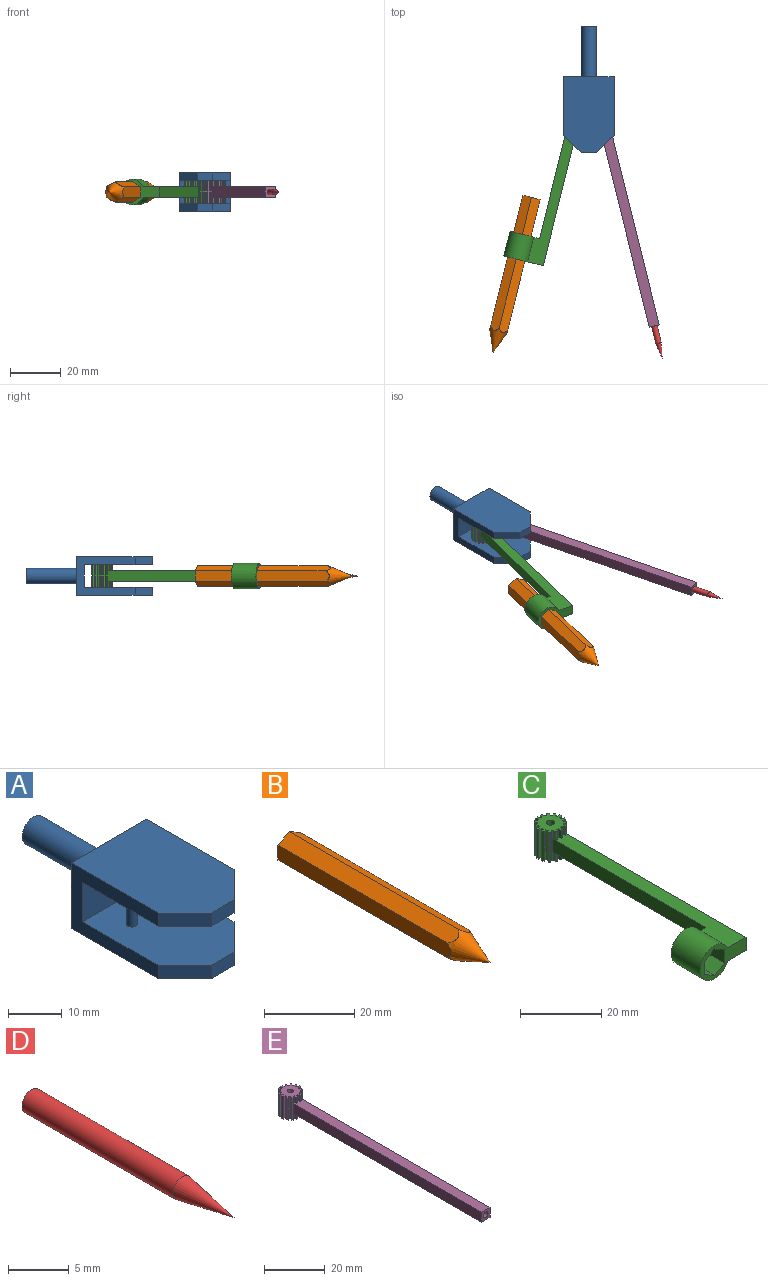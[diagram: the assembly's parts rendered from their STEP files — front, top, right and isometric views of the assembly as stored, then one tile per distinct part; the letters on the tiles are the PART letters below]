
ASSEMBLY  parts=5 mates=4
PART A: 18 faces, bbox 20x50x15 mm
  f0: plane 6x3mm, normal (0,-1,0), area 18mm2, adj f5,f7,f10,f11
  f1: plane 6x3mm, normal (0,-1,0), area 18mm2, adj f2,f6,f12,f13
  f2: plane 30x20mm, normal (0,0,1), area 551mm2, adj f1,f3,f4,f8,f12,f13
  f3: plane 23x15mm, normal (-1,0,0), area 165mm2, adj f2,f5,f6,f7,f8,f9,f10,f12
  f4: plane 23x15mm, normal (1,0,0), area 165mm2, adj f2,f5,f6,f7,f8,f9,f11,f13
  f5: plane 30x20mm, normal (0,0,-1), area 551mm2, adj f0,f3,f4,f8,f10,f11
  f6: plane 27x20mm, normal (0,0,-1), area 484.7mm2, adj f1,f3,f4,f9,f12,f13,f14,f15
  f7: plane 27x20mm, normal (0,0,1), area 484.7mm2, adj f0,f3,f4,f9,f10,f11,f14,f15
  f8: plane 20x15mm, normal (0,1,0), area 271.7mm2, adj f2,f3,f4,f5,f16
  f9: plane 20x9mm, normal (0,-1,0), area 180mm2, adj f3,f4,f6,f7
  f10: plane 7x7mm, normal (-0.71,-0.71,0), area 29.7mm2, adj f0,f3,f5,f7
  f11: plane 7x7mm, normal (0.71,-0.71,0), area 29.7mm2, adj f0,f4,f5,f7
  f12: plane 7x7mm, normal (-0.71,-0.71,0), area 29.7mm2, adj f1,f2,f3,f6
  f13: plane 7x7mm, normal (0.71,-0.71,0), area 29.7mm2, adj f1,f2,f4,f6
  f14: cylinder r=1mm len=9mm, axis (0,0,1), area 56.5mm2, adj f6,f7
  f15: cylinder r=1mm len=9mm, axis (0,0,1), area 56.5mm2, adj f6,f7
  f16: cylinder r=3mm len=20mm, axis (0,-1,0), area 377mm2, adj f8,f17
  f17: plane 6x6mm, normal (0,1,0), area 28.3mm2, adj f16
PART B: 8 faces, bbox 8x63x8 mm
  f0: plane 54.43x4mm, normal (1,0,0), area 215.9mm2, adj f1,f4,f6,f7
  f1: plane 54.43x3.46mm, normal (0.5,0,0.87), area 215.9mm2, adj f0,f2,f6,f7
  f2: plane 54.43x3.46mm, normal (-0.5,0,0.87), area 215.9mm2, adj f1,f3,f6,f7
  f3: plane 54.43x4mm, normal (-1,0,0), area 215.9mm2, adj f2,f5,f6,f7
  f4: plane 54.43x3.46mm, normal (0.5,0,-0.87), area 215.9mm2, adj f0,f5,f6,f7
  f5: plane 54.43x3.46mm, normal (-0.5,0,-0.87), area 215.9mm2, adj f3,f4,f6,f7
  f6: plane 8x6.93mm, normal (0,1,0), area 41.6mm2, adj f0,f1,f2,f3,f4,f5
  f7: cone r=40mm half-angle=22deg, axis (0,1,0), area 111mm2, adj f0,f1,f2,f3,f4,f5
PART C: 87 faces, bbox 18.1x70x10 mm
  f0: cylinder r=3.25mm len=9mm, axis (0,0,-1), area 3.5mm2, adj f1,f13,f27,f28,f73,f74,f78,f79
  f1: plane 2.5x0.79mm, normal (0.96,0.29,0), area 2.1mm2, adj f0,f2,f73,f78
  f2: plane 2.5x0.55mm, normal (0.41,-0.91,0), area 1.5mm2, adj f1,f3,f73,f78
  f3: plane 2.5x0.71mm, normal (-0.86,-0.51,0), area 2.1mm2, adj f2,f4,f73,f78
  f4: cylinder r=3.25mm len=2.5mm, axis (0,0,-1), area 1.4mm2, adj f3,f5,f73,f78
  f5: plane 2.5x0.82mm, normal (0.99,-0.12,0), area 2.1mm2, adj f4,f6,f73,f78
  f6: plane 2.5x0.6mm, normal (0,-1,0), area 1.5mm2, adj f5,f7,f73,f78
  f7: plane 2.5x0.82mm, normal (-0.99,-0.12,0), area 2.1mm2, adj f6,f8,f73,f78
  f8: cylinder r=3.25mm len=2.5mm, axis (0,0,-1), area 1.4mm2, adj f7,f9,f73,f78
  f9: plane 2.5x0.71mm, normal (0.86,-0.51,0), area 2.1mm2, adj f8,f10,f73,f78
  f10: plane 2.5x0.55mm, normal (-0.41,-0.91,0), area 1.5mm2, adj f9,f11,f73,f78
  f11: plane 2.5x0.79mm, normal (-0.96,0.29,0), area 2.1mm2, adj f10,f12,f73,f78
  f12: cylinder r=3.25mm len=9mm, axis (0,0,-1), area 3.5mm2, adj f11,f13,f38,f39,f73,f75,f78,f79
  f13: plane 8.12x8.07mm, normal (0,0,1), area 38.5mm2, adj f0,f12,f14,f15,f16,f17,f18,f19
  f14: plane 9x0.52mm, normal (0.87,0.5,0), area 5.4mm2, adj f13,f15,f71,f73
  f15: plane 9x0.66mm, normal (0.6,-0.8,0), area 7.5mm2, adj f13,f14,f16,f73
  f16: cylinder r=3.25mm len=9mm, axis (0,0,-1), area 5mm2, adj f13,f15,f17,f73
  f17: plane 9x0.83mm, normal (0.02,1,0), area 7.5mm2, adj f13,f16,f18,f73
  f18: plane 9x0.6mm, normal (0.99,0.1,0), area 5.4mm2, adj f13,f17,f19,f73
  f19: plane 9x0.81mm, normal (0.22,-0.97,0), area 7.5mm2, adj f13,f18,f20,f73
  f20: cylinder r=3.25mm len=9mm, axis (0,0,-1), area 5mm2, adj f13,f19,f21,f73
  f21: plane 9x0.75mm, normal (0.42,0.91,0), area 7.5mm2, adj f13,f20,f22,f73
  f22: plane 9x0.57mm, normal (0.95,-0.31,0), area 5.4mm2, adj f13,f21,f23,f73
  f23: plane 9x0.82mm, normal (-0.19,-0.98,0), area 7.5mm2, adj f13,f22,f24,f73
  f24: cylinder r=3.25mm len=9mm, axis (0,0,-1), area 5mm2, adj f13,f23,f25,f73
  f25: plane 9x0.63mm, normal (0.75,0.66,0), area 7.5mm2, adj f13,f24,f26,f73
  f26: plane 9x0.45mm, normal (0.74,-0.67,0), area 5.4mm2, adj f13,f25,f27,f73
  f27: plane 9x0.68mm, normal (-0.57,-0.82,0), area 7.5mm2, adj f0,f13,f26,f73
  f28: plane 2.5x0.79mm, normal (0.96,0.29,0), area 2.1mm2, adj f0,f13,f29,f79
  f29: plane 2.5x0.55mm, normal (0.41,-0.91,0), area 1.5mm2, adj f13,f28,f30,f79
  f30: plane 2.5x0.71mm, normal (-0.86,-0.51,0), area 2.1mm2, adj f13,f29,f31,f79
  f31: cylinder r=3.25mm len=2.5mm, axis (0,0,-1), area 1.4mm2, adj f13,f30,f32,f79
  f32: plane 2.5x0.82mm, normal (0.99,-0.12,0), area 2.1mm2, adj f13,f31,f33,f79
  f33: plane 2.5x0.6mm, normal (0,-1,0), area 1.5mm2, adj f13,f32,f34,f79
  f34: plane 2.5x0.82mm, normal (-0.99,-0.12,0), area 2.1mm2, adj f13,f33,f35,f79
  f35: cylinder r=3.25mm len=2.5mm, axis (0,0,-1), area 1.4mm2, adj f13,f34,f36,f79
  f36: plane 2.5x0.71mm, normal (0.86,-0.51,0), area 2.1mm2, adj f13,f35,f37,f79
  f37: plane 2.5x0.55mm, normal (-0.41,-0.91,0), area 1.5mm2, adj f13,f36,f38,f79
  f38: plane 2.5x0.79mm, normal (-0.96,0.29,0), area 2.1mm2, adj f12,f13,f37,f79
  f39: plane 9x0.68mm, normal (0.57,-0.82,0), area 7.5mm2, adj f12,f13,f40,f73
  f40: plane 9x0.45mm, normal (-0.74,-0.67,0), area 5.4mm2, adj f13,f39,f41,f73
  f41: plane 9x0.63mm, normal (-0.75,0.66,0), area 7.5mm2, adj f13,f40,f42,f73
  f42: cylinder r=3.25mm len=9mm, axis (0,0,-1), area 5mm2, adj f13,f41,f43,f73
  f43: plane 9x0.82mm, normal (0.19,-0.98,0), area 7.5mm2, adj f13,f42,f44,f73
  f44: plane 9x0.57mm, normal (-0.95,-0.31,0), area 5.4mm2, adj f13,f43,f45,f73
  f45: plane 9x0.75mm, normal (-0.42,0.91,0), area 7.5mm2, adj f13,f44,f46,f73
  f46: cylinder r=3.25mm len=9mm, axis (0,0,-1), area 5mm2, adj f13,f45,f47,f73
  f47: plane 9x0.81mm, normal (-0.22,-0.97,0), area 7.5mm2, adj f13,f46,f48,f73
  f48: plane 9x0.6mm, normal (-0.99,0.1,0), area 5.4mm2, adj f13,f47,f49,f73
  f49: plane 9x0.83mm, normal (-0.02,1,0), area 7.5mm2, adj f13,f48,f50,f73
  f50: cylinder r=3.25mm len=9mm, axis (0,0,-1), area 5mm2, adj f13,f49,f51,f73
  f51: plane 9x0.66mm, normal (-0.6,-0.8,0), area 7.5mm2, adj f13,f50,f52,f73
  f52: plane 9x0.52mm, normal (-0.87,0.5,0), area 5.4mm2, adj f13,f51,f53,f73
  f53: plane 9x0.76mm, normal (0.39,0.92,0), area 7.5mm2, adj f13,f52,f54,f73
  f54: cylinder r=3.25mm len=9mm, axis (0,0,-1), area 5mm2, adj f13,f53,f55,f73
  f55: plane 9x0.73mm, normal (-0.87,-0.49,0), area 7.5mm2, adj f13,f54,f56,f73
  f56: plane 9x0.49mm, normal (-0.59,0.81,0), area 5.4mm2, adj f13,f55,f57,f73
  f57: plane 9x0.61mm, normal (0.73,0.68,0), area 7.5mm2, adj f13,f56,f58,f73
  f58: cylinder r=3.25mm len=9mm, axis (0,0,-1), area 5mm2, adj f13,f57,f59,f73
  f59: plane 9x0.83mm, normal (-1,-0.09,0), area 7.5mm2, adj f13,f58,f60,f73
  f60: plane 9x0.59mm, normal (-0.21,0.98,0), area 5.4mm2, adj f13,f59,f61,f73
  f61: plane 9x0.79mm, normal (0.95,0.32,0), area 7.5mm2, adj f13,f60,f62,f73
  f62: cylinder r=3.25mm len=9mm, axis (0,0,-1), area 5mm2, adj f13,f61,f63,f73
  f63: plane 9x0.79mm, normal (-0.95,0.32,0), area 7.5mm2, adj f13,f62,f64,f73
  f64: plane 9x0.59mm, normal (0.21,0.98,0), area 5.4mm2, adj f13,f63,f65,f73
  f65: plane 9x0.83mm, normal (1,-0.09,0), area 7.5mm2, adj f13,f64,f66,f73
  f66: cylinder r=3.25mm len=9mm, axis (0,0,-1), area 5mm2, adj f13,f65,f67,f73
  f67: plane 9x0.61mm, normal (-0.73,0.68,0), area 7.5mm2, adj f13,f66,f68,f73
  f68: plane 9x0.49mm, normal (0.59,0.81,0), area 5.4mm2, adj f13,f67,f69,f73
  f69: plane 9x0.73mm, normal (0.87,-0.49,0), area 7.5mm2, adj f13,f68,f70,f73
  f70: cylinder r=3.25mm len=9mm, axis (0,0,-1), area 5mm2, adj f13,f69,f71,f73
  f71: plane 9x0.76mm, normal (-0.39,0.92,0), area 7.5mm2, adj f13,f14,f70,f73
  f72: cylinder r=1mm len=9mm, axis (0,0,-1), area 56.5mm2, adj f13,f73
  f73: plane 8.12x8.07mm, normal (0,0,-1), area 38.5mm2, adj f0,f1,f2,f3,f4,f5,f6,f7
  f74: plane 63.44x4mm, normal (1,0,0), area 253.8mm2, adj f0,f76,f78,f79
  f75: plane 53.44x4mm, normal (-1,0,0), area 213.8mm2, adj f12,f77,f78,f79
  f76: plane 16x10mm, normal (0,-1,0), area 61.5mm2, adj f74,f78,f79,f80,f81,f82,f83,f84
  f77: plane 12x10mm, normal (0,1,0), area 45.5mm2, adj f75,f78,f79,f80,f81,f82,f83,f84
  f78: plane 63.44x6.42mm, normal (0,0,-1), area 274.4mm2, adj f0,f1,f2,f3,f4,f5,f6,f7
  f79: plane 63.44x6.42mm, normal (0,0,1), area 274.4mm2, adj f0,f12,f28,f29,f30,f31,f32,f33
  f80: cylinder r=5mm len=10mm, axis (0,-1,0), area 273mm2, adj f76,f77,f78,f79
  f81: plane 10x3.46mm, normal (0.5,0,0.87), area 40mm2, adj f76,f77,f82,f84
  f82: plane 10x3.46mm, normal (-0.5,0,0.87), area 40mm2, adj f76,f77,f81,f83
  f83: plane 10x4mm, normal (-1,0,0), area 40mm2, adj f76,f77,f82,f85
  f84: plane 10x4mm, normal (1,0,0), area 40mm2, adj f76,f77,f81,f86
  f85: plane 10x3.46mm, normal (-0.5,0,-0.87), area 40mm2, adj f76,f77,f83,f86
  f86: plane 10x3.46mm, normal (0.5,0,-0.87), area 40mm2, adj f76,f77,f84,f85
PART D: 3 faces, bbox 2.2x23.5x2.2 mm
  f0: cone r=1.1mm half-angle=10.4deg, axis (0,1,0), area 21.1mm2, adj f1
  f1: cylinder r=1.1mm len=17.5mm, axis (0,-1,0), area 121mm2, adj f0,f2
  f2: plane 2.2x2.2mm, normal (0,1,0), area 3.8mm2, adj f1
PART E: 79 faces, bbox 8.1x95.1x9 mm
  f0: plane 9x0.61mm, normal (-0.73,-0.68,0), area 5mm2, adj f1,f11,f24,f25,f71,f73,f74,f75
  f1: cylinder r=3.25mm len=2.5mm, axis (0,0,-1), area 1.4mm2, adj f0,f2,f11,f74
  f2: plane 2.5x0.83mm, normal (1,0.09,0), area 2.1mm2, adj f1,f3,f11,f74
  f3: plane 2.5x0.59mm, normal (0.21,-0.98,0), area 1.5mm2, adj f2,f4,f11,f74
  f4: plane 2.5x0.79mm, normal (-0.95,-0.32,0), area 2.1mm2, adj f3,f5,f11,f74
  f5: cylinder r=3.25mm len=2.5mm, axis (0,0,-1), area 1.4mm2, adj f4,f6,f11,f74
  f6: plane 2.5x0.79mm, normal (0.95,-0.32,0), area 2.1mm2, adj f5,f7,f11,f74
  f7: plane 2.5x0.59mm, normal (-0.21,-0.98,0), area 1.5mm2, adj f6,f8,f11,f74
  f8: plane 2.5x0.83mm, normal (-1,0.09,0), area 2.1mm2, adj f7,f9,f11,f74
  f9: cylinder r=3.25mm len=2.5mm, axis (0,0,-1), area 1.4mm2, adj f8,f10,f11,f74
  f10: plane 9x0.61mm, normal (0.73,-0.68,0), area 5mm2, adj f9,f11,f33,f34,f71,f72,f74,f75
  f11: plane 8.12x8.07mm, normal (0,0,1), area 38.5mm2, adj f0,f1,f2,f3,f4,f5,f6,f7
  f12: plane 9x0.57mm, normal (0.95,0.31,0), area 5.4mm2, adj f11,f13,f69,f71
  f13: plane 9x0.75mm, normal (0.42,-0.91,0), area 7.5mm2, adj f11,f12,f14,f71
  f14: cylinder r=3.25mm len=9mm, axis (0,0,-1), area 5mm2, adj f11,f13,f15,f71
  f15: plane 9x0.81mm, normal (0.22,0.97,0), area 7.5mm2, adj f11,f14,f16,f71
  f16: plane 9x0.6mm, normal (0.99,-0.1,0), area 5.4mm2, adj f11,f15,f17,f71
  f17: plane 9x0.83mm, normal (0.02,-1,0), area 7.5mm2, adj f11,f16,f18,f71
  f18: cylinder r=3.25mm len=9mm, axis (0,0,-1), area 5mm2, adj f11,f17,f19,f71
  f19: plane 9x0.66mm, normal (0.6,0.8,0), area 7.5mm2, adj f11,f18,f20,f71
  f20: plane 9x0.52mm, normal (0.87,-0.5,0), area 5.4mm2, adj f11,f19,f21,f71
  f21: plane 9x0.76mm, normal (-0.39,-0.92,0), area 7.5mm2, adj f11,f20,f22,f71
  f22: cylinder r=3.25mm len=9mm, axis (0,0,-1), area 5mm2, adj f11,f21,f23,f71
  f23: plane 9x0.73mm, normal (0.87,0.49,0), area 7.5mm2, adj f11,f22,f24,f71
  f24: plane 9x0.49mm, normal (0.59,-0.81,0), area 5.4mm2, adj f0,f11,f23,f71
  f25: cylinder r=3.25mm len=2.5mm, axis (0,0,-1), area 1.4mm2, adj f0,f26,f71,f75
  f26: plane 2.5x0.83mm, normal (1,0.09,0), area 2.1mm2, adj f25,f27,f71,f75
  f27: plane 2.5x0.59mm, normal (0.21,-0.98,0), area 1.5mm2, adj f26,f28,f71,f75
  f28: plane 2.5x0.79mm, normal (-0.95,-0.32,0), area 2.1mm2, adj f27,f29,f71,f75
  f29: cylinder r=3.25mm len=2.5mm, axis (0,0,-1), area 1.4mm2, adj f28,f30,f71,f75
  f30: plane 2.5x0.79mm, normal (0.95,-0.32,0), area 2.1mm2, adj f29,f31,f71,f75
  f31: plane 2.5x0.59mm, normal (-0.21,-0.98,0), area 1.5mm2, adj f30,f32,f71,f75
  f32: plane 2.5x0.83mm, normal (-1,0.09,0), area 2.1mm2, adj f31,f33,f71,f75
  f33: cylinder r=3.25mm len=2.5mm, axis (0,0,-1), area 1.4mm2, adj f10,f32,f71,f75
  f34: plane 9x0.49mm, normal (-0.59,-0.81,0), area 5.4mm2, adj f10,f11,f35,f71
  f35: plane 9x0.73mm, normal (-0.87,0.49,0), area 7.5mm2, adj f11,f34,f36,f71
  f36: cylinder r=3.25mm len=9mm, axis (0,0,-1), area 5mm2, adj f11,f35,f37,f71
  f37: plane 9x0.76mm, normal (0.39,-0.92,0), area 7.5mm2, adj f11,f36,f38,f71
  f38: plane 9x0.52mm, normal (-0.87,-0.5,0), area 5.4mm2, adj f11,f37,f39,f71
  f39: plane 9x0.66mm, normal (-0.6,0.8,0), area 7.5mm2, adj f11,f38,f40,f71
  f40: cylinder r=3.25mm len=9mm, axis (0,0,-1), area 5mm2, adj f11,f39,f41,f71
  f41: plane 9x0.83mm, normal (-0.02,-1,0), area 7.5mm2, adj f11,f40,f42,f71
  f42: plane 9x0.6mm, normal (-0.99,-0.1,0), area 5.4mm2, adj f11,f41,f43,f71
  f43: plane 9x0.81mm, normal (-0.22,0.97,0), area 7.5mm2, adj f11,f42,f44,f71
  f44: cylinder r=3.25mm len=9mm, axis (0,0,-1), area 5mm2, adj f11,f43,f45,f71
  f45: plane 9x0.75mm, normal (-0.42,-0.91,0), area 7.5mm2, adj f11,f44,f46,f71
  f46: plane 9x0.57mm, normal (-0.95,0.31,0), area 5.4mm2, adj f11,f45,f47,f71
  f47: plane 9x0.82mm, normal (0.19,0.98,0), area 7.5mm2, adj f11,f46,f48,f71
  f48: cylinder r=3.25mm len=9mm, axis (0,0,-1), area 5mm2, adj f11,f47,f49,f71
  f49: plane 9x0.63mm, normal (-0.75,-0.66,0), area 7.5mm2, adj f11,f48,f50,f71
  f50: plane 9x0.45mm, normal (-0.74,0.67,0), area 5.4mm2, adj f11,f49,f51,f71
  f51: plane 9x0.68mm, normal (0.57,0.82,0), area 7.5mm2, adj f11,f50,f52,f71
  f52: cylinder r=3.25mm len=9mm, axis (0,0,-1), area 5mm2, adj f11,f51,f53,f71
  f53: plane 9x0.79mm, normal (-0.96,-0.29,0), area 7.5mm2, adj f11,f52,f54,f71
  f54: plane 9x0.55mm, normal (-0.41,0.91,0), area 5.4mm2, adj f11,f53,f55,f71
  f55: plane 9x0.71mm, normal (0.86,0.51,0), area 7.5mm2, adj f11,f54,f56,f71
  f56: cylinder r=3.25mm len=9mm, axis (0,0,-1), area 5mm2, adj f11,f55,f57,f71
  f57: plane 9x0.82mm, normal (-0.99,0.12,0), area 7.5mm2, adj f11,f56,f58,f71
  f58: plane 9x0.6mm, normal (0,1,0), area 5.4mm2, adj f11,f57,f59,f71
  f59: plane 9x0.82mm, normal (0.99,0.12,0), area 7.5mm2, adj f11,f58,f60,f71
  f60: cylinder r=3.25mm len=9mm, axis (0,0,-1), area 5mm2, adj f11,f59,f61,f71
  f61: plane 9x0.71mm, normal (-0.86,0.51,0), area 7.5mm2, adj f11,f60,f62,f71
  f62: plane 9x0.55mm, normal (0.41,0.91,0), area 5.4mm2, adj f11,f61,f63,f71
  f63: plane 9x0.79mm, normal (0.96,-0.29,0), area 7.5mm2, adj f11,f62,f64,f71
  f64: cylinder r=3.25mm len=9mm, axis (0,0,-1), area 5mm2, adj f11,f63,f65,f71
  f65: plane 9x0.68mm, normal (-0.57,0.82,0), area 7.5mm2, adj f11,f64,f66,f71
  f66: plane 9x0.45mm, normal (0.74,0.67,0), area 5.4mm2, adj f11,f65,f67,f71
  f67: plane 9x0.63mm, normal (0.75,-0.66,0), area 7.5mm2, adj f11,f66,f68,f71
  f68: cylinder r=3.25mm len=9mm, axis (0,0,-1), area 5mm2, adj f11,f67,f69,f71
  f69: plane 9x0.82mm, normal (-0.19,0.98,0), area 7.5mm2, adj f11,f12,f68,f71
  f70: cylinder r=1mm len=9mm, axis (0,0,-1), area 56.5mm2, adj f11,f71
  f71: plane 8.12x8.07mm, normal (0,0,-1), area 38.5mm2, adj f0,f10,f12,f13,f14,f15,f16,f17
  f72: plane 87.7x4mm, normal (-1,0,0), area 350.8mm2, adj f10,f74,f75,f76
  f73: plane 87.7x4mm, normal (1,0,0), area 350.8mm2, adj f0,f74,f75,f76
  f74: plane 88.16x4mm, normal (0,0,1), area 350.4mm2, adj f0,f1,f2,f3,f4,f5,f6,f7
  f75: plane 88.16x4mm, normal (0,0,-1), area 350.4mm2, adj f0,f10,f25,f26,f27,f28,f29,f30
  f76: plane 4x4mm, normal (0,-1,0), area 12.2mm2, adj f72,f73,f74,f75,f77
  f77: cylinder r=1.1mm len=10.5mm, axis (0,-1,0), area 72.6mm2, adj f76,f78
  f78: plane 2.2x2.2mm, normal (0,-1,0), area 3.8mm2, adj f77
PLACE A t=(-7.46,18.96,-3.69)mm fixed
PLACE B rot(axis=(0,0,-1),13.9deg) t=(-8.77,18.15,-3.69)mm
PLACE C rot(axis=(0,0,-1),13.9deg) t=(-8.77,18.15,-3.69)mm
PLACE D rot(axis=(0,0,1),13.9deg) t=(-6.14,18.15,-3.69)mm
PLACE E rot(axis=(0,0,1),13.9deg) t=(-6.14,18.15,-3.69)mm
MATE revolute C.f0 <-> A.f15  axis (0,0,1) through (-11.46,23.96,0.81)mm
MATE fastened E.f77 <-> D.f1  axis (0.24,-0.97,0) through (15.88,-54.18,-3.69)mm
MATE revolute E.f1 <-> A.f14  axis (0,0,1) through (-3.46,23.96,0.81)mm
MATE fastened B.f7 <-> C.f80  axis (0.24,0.97,0) through (-30.04,-13.68,-3.69)mm
